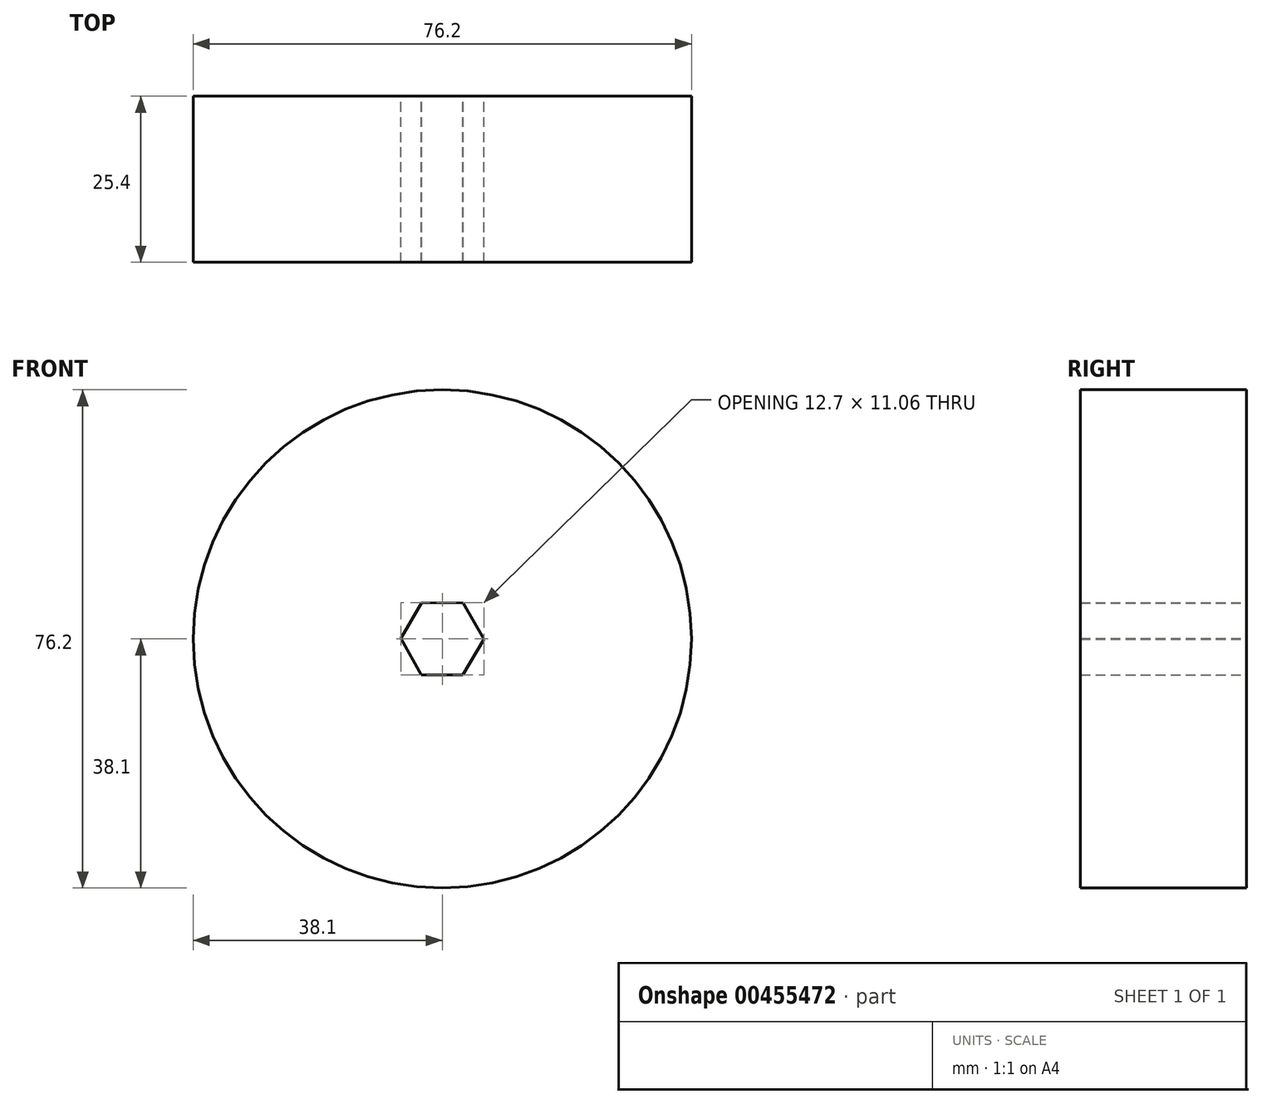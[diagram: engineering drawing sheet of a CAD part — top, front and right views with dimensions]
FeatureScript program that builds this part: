
annotation { "Feature Type Name" : "Feature", "Feature Type Description" : "" }
export const myFeature = defineFeature(function(context is Context, id is Id, definition is map)
    precondition{}
    {
        {
            var Q0;
            Q0=qCreatedBy(makeId("Front.planeOp"),FACE);
            var sketch = newSketch(context, id + "F0", { "sketchPlane" : qUnion([Q0])});
            skCircle(sketch, "E0", {"center": v(0, 0) * mm, "radius": 38.1 * mm});
            skCircle(sketch, "E1.cCircle", {"center": v(0, 0) * mm, "radius": 6.35 * mm, "construction": true});
            skLineSegment(sketch, "E1.0", {"start": v(3.22, 5.47) * mm, "end": v(6.35, -0.06) * mm});
            skLineSegment(sketch, "E1.1", {"start": v(6.35, -0.06) * mm, "end": v(3.13, -5.53) * mm});
            skLineSegment(sketch, "E1.2", {"start": v(3.13, -5.53) * mm, "end": v(-3.22, -5.47) * mm});
            skLineSegment(sketch, "E1.3", {"start": v(-3.22, -5.47) * mm, "end": v(-6.35, 0.06) * mm});
            skLineSegment(sketch, "E1.4", {"start": v(-6.35, 0.06) * mm, "end": v(-3.13, 5.53) * mm});
            skLineSegment(sketch, "E1.5", {"start": v(-3.13, 5.53) * mm, "end": v(3.22, 5.47) * mm});
            skSolve(sketch);
        }
        {
            var Q0;
            Q0=makeQuery(id+"F0.imprint","IMPRINT",FACE,{"disambiguationData":[TD([[makeQuery(id+"F0.imprint","IMPRINT",EDGE,{"derivedFrom":sQuery(id+"F0.wireOp",EDGE,"E0")}),1.0]])]});
            extrude(context, id + "F1", {"entities" : qUnion([Q0]), "endBound" : BoundingType.SYMMETRIC, "depth" : 25.4 * mm});
        }
    });
